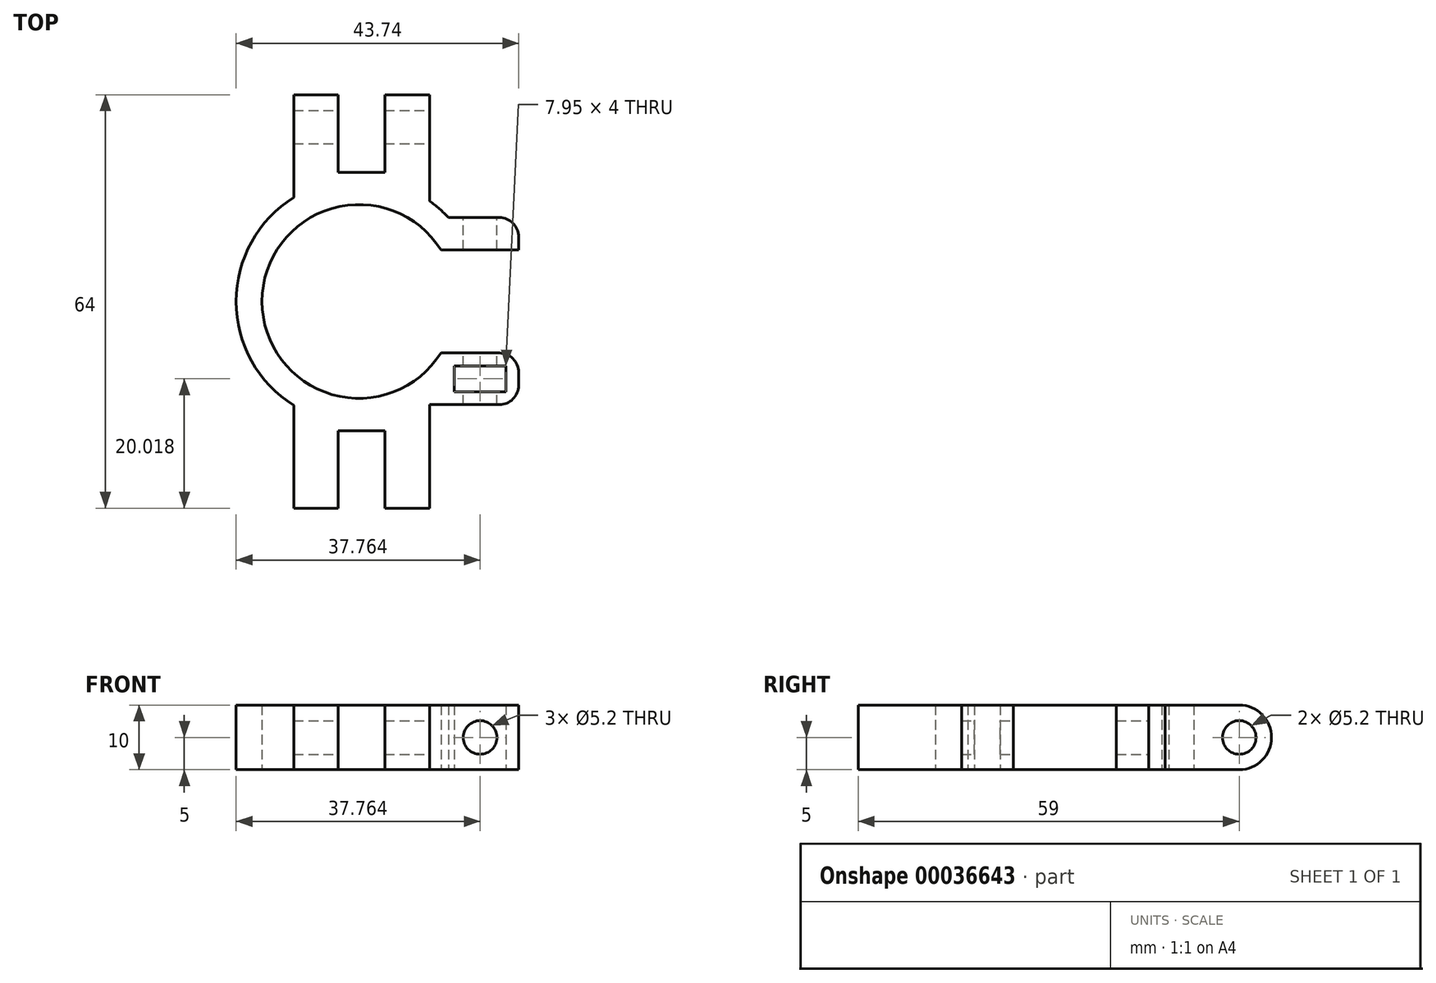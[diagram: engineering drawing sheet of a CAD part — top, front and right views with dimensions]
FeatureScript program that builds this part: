
annotation { "Feature Type Name" : "Feature", "Feature Type Description" : "" }
export const myFeature = defineFeature(function(context is Context, id is Id, definition is map)
    precondition{}
    {
        {
            var Q0;
            Q0=qCreatedBy(makeId("Top.planeOp"),FACE);
            var sketch = newSketch(context, id + "F0", { "sketchPlane" : qUnion([Q0])});
            skArc(sketch, "E0", {"start": v(13.87, 12.98) * mm, "mid": v(12.46, 14.34) * mm, "end": v(10.92, 15.55) * mm});
            skLineSegment(sketch, "E1.rect.top", {"start": v(24.74, 12.98) * mm, "end": v(13.87, 12.98) * mm});
            skLineSegment(sketch, "E1.rect.left", {"start": v(24.74, -15.98) * mm, "end": v(24.74, -7.98) * mm});
            skLineSegment(sketch, "E2.0", {"start": v(24.74, 7.98) * mm, "end": v(12.7, 7.98) * mm});
            skLineSegment(sketch, "E3.0", {"start": v(24.74, -7.98) * mm, "end": v(12.7, -7.98) * mm});
            skLineSegment(sketch, "E4.trimOffspring", {"start": v(24.74, 7.98) * mm, "end": v(24.74, 12.98) * mm});
            skCircle(sketch, "E5.converted", {"center": v(0, 0) * mm, "radius": 15 * mm, "construction": true});
            skArc(sketch, "E6.0", {"start": v(12.7, 7.98) * mm, "mid": v(-15, 0) * mm, "end": v(12.7, -7.98) * mm});
            skLineSegment(sketch, "E7.rect.bottom", {"start": v(-10.08, 32) * mm, "end": v(-3.18, 32) * mm});
            skLineSegment(sketch, "E7.rect.left", {"start": v(-10.08, 32) * mm, "end": v(-10.08, 16.1) * mm});
            skLineSegment(sketch, "E7.rect.right", {"start": v(10.92, 32) * mm, "end": v(10.92, 15.55) * mm});
            skPoint(sketch, "E7.rect.middle", {"position": v(0.06, 0.12) * mm});
            skLineSegment(sketch, "E8.0", {"start": v(-3.18, 20) * mm, "end": v(4.02, 20) * mm});
            skLineSegment(sketch, "E9.0", {"start": v(-3.18, 32) * mm, "end": v(-3.18, 18.73) * mm});
            skLineSegment(sketch, "E10.0", {"start": v(4.02, 32) * mm, "end": v(4.02, 18.57) * mm});
            skArc(sketch, "E11.trimOffspring", {"start": v(-10.08, 16.1) * mm, "mid": v(-16.04, -10.18) * mm, "end": v(10.27, -15.98) * mm});
            skLineSegment(sketch, "E12.trimOffspring", {"start": v(4.02, 32) * mm, "end": v(10.92, 32) * mm});
            skLineSegment(sketch, "E13.0", {"start": v(24.74, -15.98) * mm, "end": v(12.7, -15.98) * mm});
            skLineSegment(sketch, "E14", {"start": v(12.7, -15.98) * mm, "end": v(10.27, -15.98) * mm});
            skLineSegment(sketch, "E15.0", {"start": v(22.74, -13.98) * mm, "end": v(22.74, -9.98) * mm});
            skLineSegment(sketch, "E16.0", {"start": v(14.79, -13.98) * mm, "end": v(14.79, -9.98) * mm});
            skLineSegment(sketch, "E17", {"start": v(24.74, -7.98) * mm, "end": v(24.74, 7.98) * mm, "construction": true});
            skLineSegment(sketch, "E18.0", {"start": v(22.74, -13.98) * mm, "end": v(14.79, -13.98) * mm});
            skLineSegment(sketch, "E19.0", {"start": v(22.74, -9.98) * mm, "end": v(14.79, -9.98) * mm});
            skLineSegment(sketch, "E20", {"start": v(0, 0) * mm, "end": v(-27.28, 0) * mm, "construction": true});
            skLineSegment(sketch, "E21.MirrorCS", {"start": v(-3.18, -32) * mm, "end": v(-3.18, -18.73) * mm});
            skLineSegment(sketch, "E22.MirrorCS", {"start": v(-3.18, -20) * mm, "end": v(4.02, -20) * mm});
            skLineSegment(sketch, "E23.MirrorCS", {"start": v(10.92, -32) * mm, "end": v(10.92, -15.55) * mm});
            skLineSegment(sketch, "E24.MirrorCS", {"start": v(-10.08, -32) * mm, "end": v(-10.08, -16.1) * mm});
            skLineSegment(sketch, "E25.MirrorCS", {"start": v(-10.08, -32) * mm, "end": v(-3.18, -32) * mm});
            skLineSegment(sketch, "E26.MirrorCS", {"start": v(4.02, -32) * mm, "end": v(10.92, -32) * mm});
            skLineSegment(sketch, "E27.MirrorCS", {"start": v(4.02, -32) * mm, "end": v(4.02, -18.57) * mm});
            skSolve(sketch);
        }
        {
            var Q0;
            Q0 = qSketchRegion(id + "F0", true);
            extrude(context, id + "F1", {"entities" : qUnion([Q0]), "depth" : 10 * mm});
        }
        {
            var Q0;
            Q0=makeQuery(id+"F1.opExtrude","SWEPT_FACE",FACE,{"disambiguationData":[OSD([sQuery(id+"F0.wireOp",EDGE,"E7.rect.right")])]});
            var sketch = newSketch(context, id + "F2", { "sketchPlane" : qUnion([Q0])});
            skLineSegment(sketch, "E28.0.0", {"start": v(27, 0) * mm, "end": v(32, 0) * mm});
            skLineSegment(sketch, "E28.0.1", {"start": v(32, 0) * mm, "end": v(32, 10) * mm});
            skLineSegment(sketch, "E28.0.2", {"start": v(32, 10) * mm, "end": v(27, 10) * mm});
            skCircle(sketch, "E29", {"center": v(27, 5) * mm, "radius": 2.6 * mm});
            skPoint(sketch, "E29.centerSnap0", {"position": v(27, 10) * mm});
            skArc(sketch, "E30", {"start": v(27, 0) * mm, "mid": v(32, 5) * mm, "end": v(27, 10) * mm});
            skSolve(sketch);
        }
        {
            var Q0;
            Q0 = qSketchRegion(id + "F2", true);
            var Q1;
            Q1=makeQuery(id+"F1.opExtrude","SWEPT_FACE",FACE,{"disambiguationData":[OSD([sQuery(id+"F0.wireOp",EDGE,"E7.rect.left")])]});
            extrude(context, id + "F3", {"entities" : qUnion([Q0]), "operationType" : NewBodyOperationType.REMOVE, "endBound" : BoundingType.UP_TO_SURFACE, "oppositeDirection" : true, "endBoundEntityFace" : qUnion([Q1]), "depth" : 25 * mm});
        }
        {
            var Q0;
            Q0=makeQuery(id+"F1.opExtrude","SWEPT_FACE",FACE,{"disambiguationData":[OSD([sQuery(id+"F0.wireOp",EDGE,"E18.0")])]});
            var sketch = newSketch(context, id + "F4", { "sketchPlane" : qUnion([Q0])});
            skLineSegment(sketch, "E31.0.0", {"start": v(-22.74, 0) * mm, "end": v(-14.79, 0) * mm, "construction": true});
            skLineSegment(sketch, "E31.0.1", {"start": v(-14.79, 0) * mm, "end": v(-14.79, 10) * mm, "construction": true});
            skLineSegment(sketch, "E31.0.2", {"start": v(-14.79, 10) * mm, "end": v(-22.74, 10) * mm, "construction": true});
            skLineSegment(sketch, "E31.0.3", {"start": v(-22.74, 10) * mm, "end": v(-22.74, 0) * mm, "construction": true});
            skCircle(sketch, "E32", {"center": v(-18.76, 5) * mm, "radius": 2.6 * mm});
            skPoint(sketch, "E32.centerSnap0", {"position": v(-14.79, 5) * mm});
            skPoint(sketch, "E32.centerSnap1", {"position": v(-18.76, 10) * mm});
            skSolve(sketch);
        }
        {
            var Q0;
            Q0 = qSketchRegion(id + "F4", true);
            extrude(context, id + "F5", {"entities" : qUnion([Q0]), "operationType" : NewBodyOperationType.REMOVE, "endBound" : BoundingType.SYMMETRIC, "oppositeDirection" : true, "depth" : 100 * mm});
        }
        {
            var Q0;
            Q0=makeQuery(id+"F1.opExtrude","SWEPT_EDGE",EDGE,{"disambiguationData":[OSD([sQuery(id+"F0.wireOp",EDGE,"E1.rect.top"),sQuery(id+"F0.wireOp",EDGE,"E4.trimOffspring")])]});
            var Q1;
            Q1=makeQuery(id+"F1.opExtrude","SWEPT_EDGE",EDGE,{"disambiguationData":[OSD([sQuery(id+"F0.wireOp",EDGE,"E1.rect.left"),sQuery(id+"F0.wireOp",EDGE,"E3.0")])]});
            var Q2;
            Q2=makeQuery(id+"F1.opExtrude","SWEPT_EDGE",EDGE,{"disambiguationData":[OSD([sQuery(id+"F0.wireOp",EDGE,"E1.rect.left"),sQuery(id+"F0.wireOp",EDGE,"E13.0")])]});
            fillet(context, id + "F6", {"entities" : qUnion([Q0, Q1, Q2]), "radius" : 3 * mm, "tangentPropagation" : true, "allowEdgeOverflow" : false});
        }
    });
